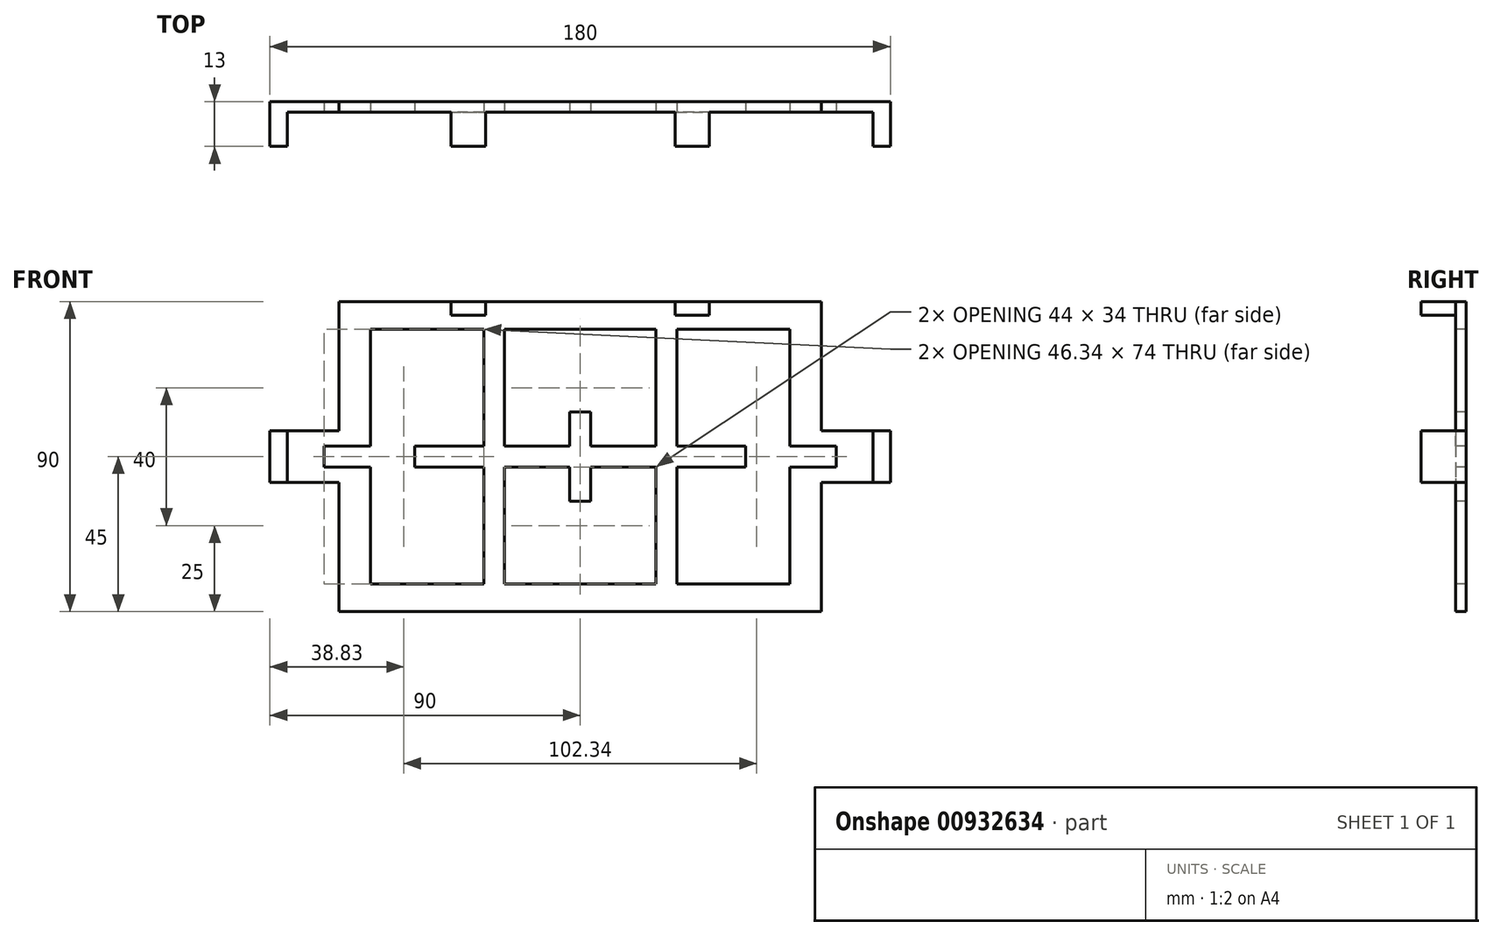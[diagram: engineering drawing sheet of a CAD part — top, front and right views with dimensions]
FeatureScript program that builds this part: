
annotation { "Feature Type Name" : "Feature", "Feature Type Description" : "" }
export const myFeature = defineFeature(function(context is Context, id is Id, definition is map)
    precondition{}
    {
        {
            var Q0;
            Q0=qCreatedBy(makeId("Front.planeOp"),FACE);
            var sketch = newSketch(context, id + "F0", { "sketchPlane" : qUnion([Q0])});
            skLineSegment(sketch, "E0.bottom", {"start": v(-70, 45) * mm, "end": v(70, 45) * mm});
            skLineSegment(sketch, "E0.top", {"start": v(-70, -45) * mm, "end": v(70, -45) * mm});
            skLineSegment(sketch, "E1.bottom", {"start": v(-70, 7.5) * mm, "end": v(-90, 7.5) * mm});
            skLineSegment(sketch, "E1.top", {"start": v(-70, -7.5) * mm, "end": v(-90, -7.5) * mm});
            skLineSegment(sketch, "E1.right", {"start": v(-90, 7.5) * mm, "end": v(-90, -7.5) * mm});
            skLineSegment(sketch, "E2", {"start": v(-70, 45) * mm, "end": v(-70, 7.5) * mm});
            skLineSegment(sketch, "E3", {"start": v(-70, -7.5) * mm, "end": v(-70, -45) * mm});
            skLineSegment(sketch, "E4", {"start": v(0, 45.83) * mm, "end": v(0, -48.86) * mm, "construction": true});
            skPoint(sketch, "E4.endSnap0", {"position": v(0, -45) * mm});
            skLineSegment(sketch, "E5.MirrorCS", {"start": v(70, 45) * mm, "end": v(70, 7.5) * mm});
            skLineSegment(sketch, "E6.MirrorCS", {"start": v(70, -7.5) * mm, "end": v(70, -45) * mm});
            skLineSegment(sketch, "E7", {"start": v(70, -7.5) * mm, "end": v(90, -7.5) * mm});
            skLineSegment(sketch, "E8", {"start": v(90, -7.5) * mm, "end": v(90, 7.5) * mm});
            skLineSegment(sketch, "E9", {"start": v(90, 7.5) * mm, "end": v(70, 7.5) * mm});
            skSolve(sketch);
        }
        {
            var Q0;
            Q0=makeQuery(id+"F0.imprint","IMPRINT",FACE,{"disambiguationData":[TD([[makeQuery(id+"F0.imprint","IMPRINT",EDGE,{"derivedFrom":sQuery(id+"F0.wireOp",EDGE,"E0.bottom")}),-1.0]])]});
            extrude(context, id + "F1", {"entities" : qUnion([Q0]), "depth" : 3 * mm, "offsetDistance" : 25 * mm});
        }
        {
            var Q0;
            Q0=makeQuery(id+"F1.opExtrude","CAP_FACE",FACE,{"disambiguationData":[OSD([sQuery(id+"F0.wireOp",EDGE,"E0.bottom"),sQuery(id+"F0.wireOp",EDGE,"E0.top"),sQuery(id+"F0.wireOp",EDGE,"E0.left"),sQuery(id+"F0.wireOp",EDGE,"E0.right")])],"isStart":false});
            var sketch = newSketch(context, id + "F2", { "sketchPlane" : qUnion([Q0])});
            skLineSegment(sketch, "E10", {"start": v(-60.8, 37) * mm, "end": v(-28, 37) * mm});
            skLineSegment(sketch, "E11", {"start": v(-28, 37) * mm, "end": v(-28, 3) * mm});
            skLineSegment(sketch, "E12", {"start": v(-28, 3) * mm, "end": v(-48, 3) * mm});
            skLineSegment(sketch, "E13", {"start": v(-28, -3) * mm, "end": v(-28, -37) * mm});
            skLineSegment(sketch, "E14", {"start": v(-28, -37) * mm, "end": v(-60.8, -37) * mm});
            skLineSegment(sketch, "E15", {"start": v(-60.8, -37) * mm, "end": v(-60.8, -3) * mm});
            skLineSegment(sketch, "E16", {"start": v(-22, 37) * mm, "end": v(-22, 3) * mm});
            skLineSegment(sketch, "E17", {"start": v(-22, 3) * mm, "end": v(-3, 3) * mm});
            skLineSegment(sketch, "E18", {"start": v(-3, -3) * mm, "end": v(-22, -3) * mm});
            skLineSegment(sketch, "E19", {"start": v(-22, -3) * mm, "end": v(-22, -37) * mm});
            skLineSegment(sketch, "E20", {"start": v(-22, -37) * mm, "end": v(0, -37) * mm});
            skLineSegment(sketch, "E21", {"start": v(-22, 37) * mm, "end": v(0, 37) * mm});
            skLineSegment(sketch, "E22", {"start": v(0, 49.32) * mm, "end": v(0, -56.6) * mm, "construction": true});
            skPoint(sketch, "E22.endSnap0", {"position": v(0, -45) * mm});
            skLineSegment(sketch, "E23.MirrorCS", {"start": v(22, 3) * mm, "end": v(3, 3) * mm});
            skLineSegment(sketch, "E24.MirrorCS", {"start": v(60.8, 37) * mm, "end": v(28, 37) * mm});
            skLineSegment(sketch, "E25.MirrorCS", {"start": v(22, -3) * mm, "end": v(22, -37) * mm});
            skLineSegment(sketch, "E26.MirrorCS", {"start": v(28, -37) * mm, "end": v(60.8, -37) * mm});
            skLineSegment(sketch, "E27.MirrorCS", {"start": v(28, 37) * mm, "end": v(28, 3) * mm});
            skLineSegment(sketch, "E28.MirrorCS", {"start": v(22, 37) * mm, "end": v(0, 37) * mm});
            skLineSegment(sketch, "E29.MirrorCS", {"start": v(3, -3) * mm, "end": v(22, -3) * mm});
            skLineSegment(sketch, "E30.MirrorCS", {"start": v(28, 3) * mm, "end": v(48, 3) * mm});
            skLineSegment(sketch, "E31.MirrorCS", {"start": v(22, 37) * mm, "end": v(22, 3) * mm});
            skLineSegment(sketch, "E32.MirrorCS", {"start": v(22, -37) * mm, "end": v(0, -37) * mm});
            skLineSegment(sketch, "E33", {"start": v(-3, 3) * mm, "end": v(-3, 13) * mm});
            skLineSegment(sketch, "E34", {"start": v(-3, 13) * mm, "end": v(0, 13) * mm});
            skLineSegment(sketch, "E35", {"start": v(-3, -3) * mm, "end": v(-3, -13) * mm});
            skLineSegment(sketch, "E36", {"start": v(-3, -13) * mm, "end": v(0, -13) * mm});
            skLineSegment(sketch, "E37.MirrorCS", {"start": v(3, 13) * mm, "end": v(0, 13) * mm});
            skLineSegment(sketch, "E38.MirrorCS", {"start": v(3, -13) * mm, "end": v(0, -13) * mm});
            skLineSegment(sketch, "E39.MirrorCS", {"start": v(3, -3) * mm, "end": v(3, -13) * mm});
            skLineSegment(sketch, "E40.MirrorCS", {"start": v(3, 3) * mm, "end": v(3, 13) * mm});
            skLineSegment(sketch, "E41", {"start": v(-94.98, 0) * mm, "end": v(101.18, 0) * mm, "construction": true});
            skLineSegment(sketch, "E42", {"start": v(-48, 3) * mm, "end": v(-48, -3) * mm});
            skLineSegment(sketch, "E43", {"start": v(-48, -3) * mm, "end": v(-28, -3) * mm});
            skPoint(sketch, "E44", {"position": v(-48, 0) * mm});
            skLineSegment(sketch, "E45.MirrorCS", {"start": v(48, -3) * mm, "end": v(28, -3) * mm});
            skLineSegment(sketch, "E46.MirrorCS", {"start": v(48, 3) * mm, "end": v(48, -3) * mm});
            skLineSegment(sketch, "E47.MirrorCS", {"start": v(28, -3) * mm, "end": v(28, -37) * mm});
            skLineSegment(sketch, "E48", {"start": v(-28, 37) * mm, "end": v(-22, 37) * mm, "construction": true});
            skLineSegment(sketch, "E49", {"start": v(-28, -37) * mm, "end": v(-22, -37) * mm, "construction": true});
            skLineSegment(sketch, "E50", {"start": v(-25, 54.06) * mm, "end": v(-25, -44.41) * mm, "construction": true});
            skPoint(sketch, "E50.startSnap0", {"position": v(-25, 37) * mm});
            skPoint(sketch, "E51", {"position": v(-25, -37) * mm});
            skLineSegment(sketch, "E52", {"start": v(-60.8, 3) * mm, "end": v(-74.34, 3) * mm});
            skLineSegment(sketch, "E53", {"start": v(-74.34, 3) * mm, "end": v(-74.34, -3) * mm});
            skLineSegment(sketch, "E54", {"start": v(-74.34, -3) * mm, "end": v(-60.8, -3) * mm});
            skLineSegment(sketch, "E55.trimOffspring", {"start": v(-60.8, 3) * mm, "end": v(-60.8, 37) * mm});
            skPoint(sketch, "E56", {"position": v(-74.34, 0) * mm});
            skLineSegment(sketch, "E57.MirrorCS", {"start": v(60.8, 3) * mm, "end": v(60.8, 37) * mm});
            skLineSegment(sketch, "E58.MirrorCS", {"start": v(60.8, 3) * mm, "end": v(74.34, 3) * mm});
            skLineSegment(sketch, "E59.MirrorCS", {"start": v(74.34, 3) * mm, "end": v(74.34, -3) * mm});
            skLineSegment(sketch, "E60.MirrorCS", {"start": v(74.34, -3) * mm, "end": v(60.8, -3) * mm});
            skLineSegment(sketch, "E61.MirrorCS", {"start": v(60.8, -37) * mm, "end": v(60.8, -3) * mm});
            skSolve(sketch);
        }
        {
            var Q0;
            Q0 = qSketchRegion(id + "F2", true);
            extrude(context, id + "F3", {"entities" : qUnion([Q0]), "operationType" : NewBodyOperationType.REMOVE, "oppositeDirection" : true, "depth" : 25 * mm, "offsetDistance" : 25 * mm});
        }
        {
            var Q0;
            Q0=makeQuery(id+"F1.opExtrude","CAP_FACE",FACE,{"disambiguationData":[OSD([sQuery(id+"F0.wireOp",EDGE,"E0.bottom"),sQuery(id+"F0.wireOp",EDGE,"E0.top"),sQuery(id+"F0.wireOp",EDGE,"E0.right"),sQuery(id+"F0.wireOp",EDGE,"E1.bottom"),sQuery(id+"F0.wireOp",EDGE,"E1.top"),sQuery(id+"F0.wireOp",EDGE,"E1.right"),sQuery(id+"F0.wireOp",EDGE,"E2"),sQuery(id+"F0.wireOp",EDGE,"E3")])],"isStart":false});
            var sketch = newSketch(context, id + "F4", { "sketchPlane" : qUnion([Q0])});
            skLineSegment(sketch, "E62.bottom", {"start": v(-90, 7.5) * mm, "end": v(-85, 7.5) * mm});
            skLineSegment(sketch, "E62.top", {"start": v(-90, -7.5) * mm, "end": v(-85, -7.5) * mm});
            skLineSegment(sketch, "E62.left", {"start": v(-90, 7.5) * mm, "end": v(-90, -7.5) * mm});
            skLineSegment(sketch, "E62.right", {"start": v(-85, 7.5) * mm, "end": v(-85, -7.5) * mm});
            skLineSegment(sketch, "E63", {"start": v(0, 49.36) * mm, "end": v(0, -47.8) * mm, "construction": true});
            skPoint(sketch, "E63.startSnap0", {"position": v(0, 45) * mm});
            skLineSegment(sketch, "E64.MirrorCS", {"start": v(85, 7.5) * mm, "end": v(85, -7.5) * mm});
            skLineSegment(sketch, "E65.MirrorCS", {"start": v(90, 7.5) * mm, "end": v(85, 7.5) * mm});
            skLineSegment(sketch, "E66.MirrorCS", {"start": v(90, 7.5) * mm, "end": v(90, -7.5) * mm});
            skLineSegment(sketch, "E67.MirrorCS", {"start": v(90, -7.5) * mm, "end": v(85, -7.5) * mm});
            skLineSegment(sketch, "E68.bottom", {"start": v(-37.5, 45) * mm, "end": v(-27.5, 45) * mm});
            skLineSegment(sketch, "E68.top", {"start": v(-37.5, 41) * mm, "end": v(-27.5, 41) * mm});
            skLineSegment(sketch, "E68.left", {"start": v(-37.5, 45) * mm, "end": v(-37.5, 41) * mm});
            skLineSegment(sketch, "E68.right", {"start": v(-27.5, 45) * mm, "end": v(-27.5, 41) * mm});
            skLineSegment(sketch, "E69.MirrorCS", {"start": v(37.5, 41) * mm, "end": v(27.5, 41) * mm});
            skLineSegment(sketch, "E70.MirrorCS", {"start": v(27.5, 45) * mm, "end": v(27.5, 41) * mm});
            skLineSegment(sketch, "E71.MirrorCS", {"start": v(37.5, 45) * mm, "end": v(27.5, 45) * mm});
            skLineSegment(sketch, "E72.MirrorCS", {"start": v(37.5, 45) * mm, "end": v(37.5, 41) * mm});
            skSolve(sketch);
        }
        {
            var Q0;
            Q0=makeQuery(id+"F4.imprint","IMPRINT",FACE,{"disambiguationData":[TD([[makeQuery(id+"F4.imprint","IMPRINT",EDGE,{"derivedFrom":sQuery(id+"F4.wireOp",EDGE,"E62.bottom")}),1.0]])]});
            var Q1;
            Q1=makeQuery(id+"F4.imprint","IMPRINT",FACE,{"disambiguationData":[TD([[makeQuery(id+"F4.imprint","IMPRINT",EDGE,{"derivedFrom":sQuery(id+"F4.wireOp",EDGE,"E64.MirrorCS")}),1.0]])]});
            var Q2;
            Q2=makeQuery(id+"F4.imprint","IMPRINT",FACE,{"disambiguationData":[TD([[makeQuery(id+"F4.imprint","IMPRINT",EDGE,{"derivedFrom":sQuery(id+"F4.wireOp",EDGE,"E68.bottom")}),-1.0]])]});
            var Q3;
            Q3=makeQuery(id+"F4.imprint","IMPRINT",FACE,{"disambiguationData":[TD([[makeQuery(id+"F4.imprint","IMPRINT",EDGE,{"derivedFrom":sQuery(id+"F4.wireOp",EDGE,"E69.MirrorCS")}),-1.0]])]});
            extrude(context, id + "F5", {"entities" : qUnion([Q0, Q1, Q2, Q3]), "operationType" : NewBodyOperationType.ADD, "depth" : 10 * mm, "offsetDistance" : 25 * mm});
        }
    });
